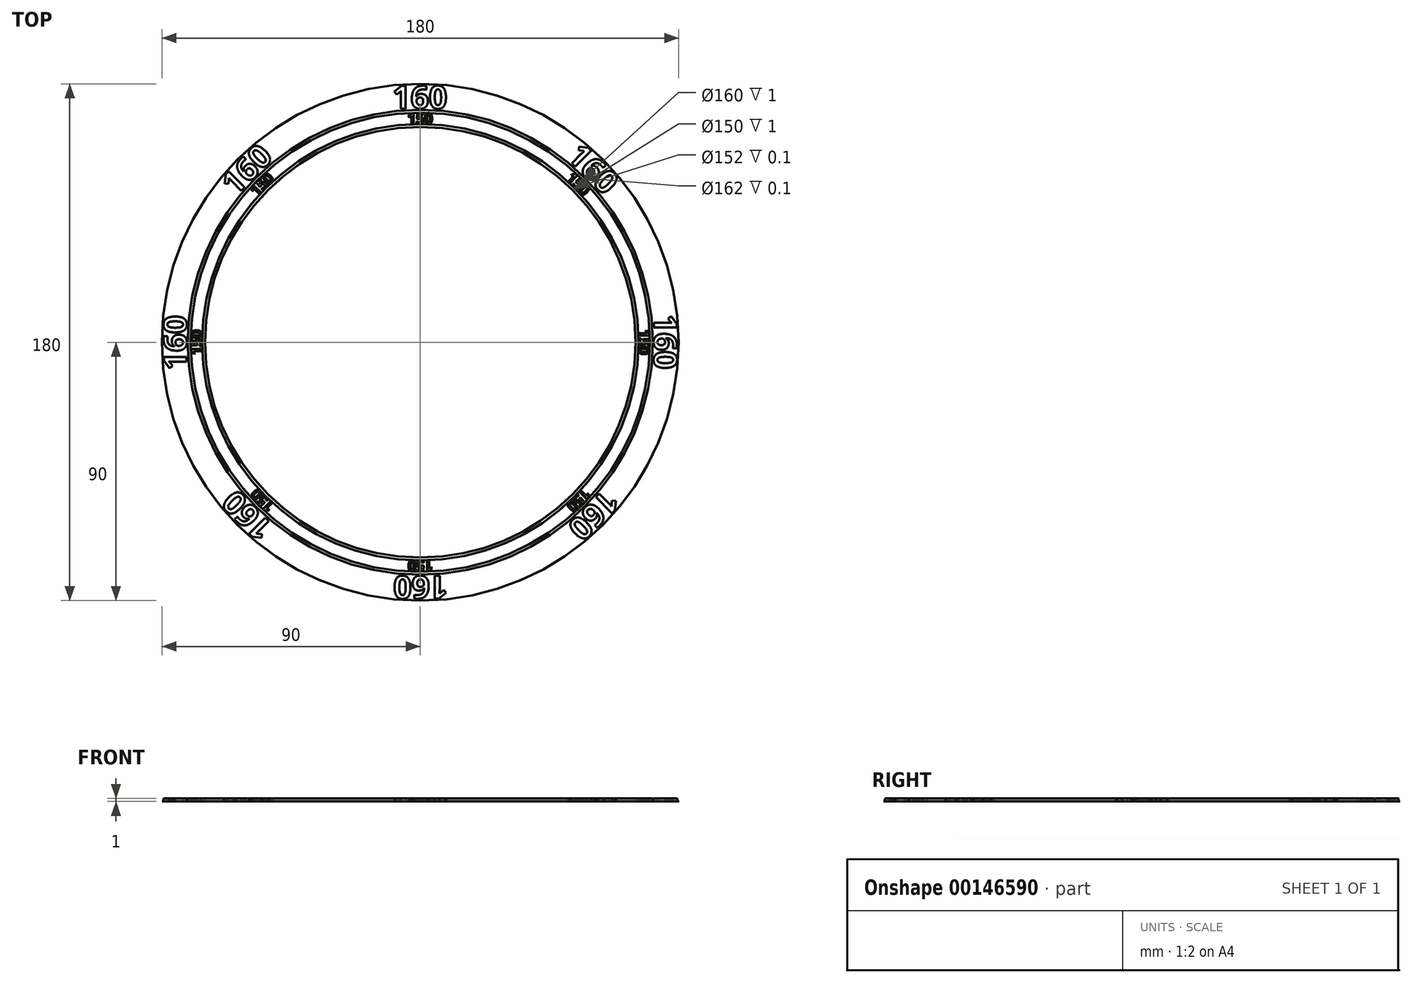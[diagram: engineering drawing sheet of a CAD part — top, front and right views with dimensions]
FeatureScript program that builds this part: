
annotation { "Feature Type Name" : "Feature", "Feature Type Description" : "" }
export const myFeature = defineFeature(function(context is Context, id is Id, definition is map)
    precondition{}
    {
        {
            var Q0;
            Q0=qCreatedBy(makeId("Top.planeOp"),FACE);
            var sketch = newSketch(context, id + "F0", { "sketchPlane" : qUnion([Q0])});
            skCircle(sketch, "E0", {"center": v(0, 0) * mm, "radius": 80 * mm});
            skCircle(sketch, "E1", {"center": v(0, 0) * mm, "radius": 75 * mm});
            skCircle(sketch, "E2", {"center": v(0, 0) * mm, "radius": 90 * mm});
            skCircle(sketch, "E3", {"center": v(0, 0) * mm, "radius": 100 * mm});
            skCircle(sketch, "E4", {"center": v(0, 0) * mm, "radius": 76 * mm});
            skCircle(sketch, "E5", {"center": v(0, 0) * mm, "radius": 81 * mm});
            skCircle(sketch, "E6", {"center": v(0, 0) * mm, "radius": 91 * mm});
            skSolve(sketch);
        }
        {
            var Q0;
            Q0=makeQuery(id+"F0.imprint","IMPRINT",FACE,{"disambiguationData":[TD([[makeQuery(id+"F0.imprint","IMPRINT",EDGE,{"derivedFrom":sQuery(id+"F0.wireOp",EDGE,"E1")}),-1.0]])]});
            var Q1;
            Q1=makeQuery(id+"F0.imprint","IMPRINT",FACE,{"disambiguationData":[TD([[makeQuery(id+"F0.imprint","IMPRINT",EDGE,{"derivedFrom":sQuery(id+"F0.wireOp",EDGE,"E0")}),-1.0]])]});
            extrude(context, id + "F1", {"entities" : qUnion([Q0, Q1]), "depth" : 1 * mm});
        }
        {
            var Q0;
            Q0=makeQuery(id+"F0.imprint","IMPRINT",FACE,{"disambiguationData":[TD([[makeQuery(id+"F0.imprint","IMPRINT",EDGE,{"derivedFrom":sQuery(id+"F0.wireOp",EDGE,"E1")}),1.0]])]});
            var sketch = newSketch(context, id + "F2", { "sketchPlane" : qUnion([Q0])});
            skText(sketch, "E7", { "text": "150", "fontName": "OpenSans-Bold.ttf"});
            skText(sketch, "E8", { "text": "160", "fontName": "OpenSans-Bold.ttf"});
            const initialGuessF2  = {"E7": [-0.00447, 0.07608, 1, 0, 0.0037], "E8": [-0.00968, 0.08139, 1, 0, 0.008]};
            skSetInitialGuess(sketch, initialGuessF2);
            skSolve(sketch);
        }
        {
            var Q0;
            Q0 = qSketchRegion(id + "F2", true);
            var Q1;
            Q1 = qConstructionFilter(qBodyType(qCreatedBy(id + "F2" ,EDGE), BodyType.WIRE), ConstructionObject.NO);
            extrude(context, id + "F3", {"entities" : qUnion([Q0]), "surfaceEntities" : qUnion([Q1]), "depth" : 1 * mm});
        }
        {
            var Q0;
            Q0=makeQuery(id+"F3.opExtrude","SWEPT_BODY",BODY,{"disambiguationData":[OSD([sQuery(id+"F2.wireOp",EDGE,"E8.sketch_text.stroke-35"),sQuery(id+"F2.wireOp",EDGE,"E8.sketch_text.stroke-36"),sQuery(id+"F2.wireOp",EDGE,"E8.sketch_text.stroke-37"),sQuery(id+"F2.wireOp",EDGE,"E8.sketch_text.stroke-38"),sQuery(id+"F2.wireOp",EDGE,"E8.sketch_text.stroke-39"),sQuery(id+"F2.wireOp",EDGE,"E8.sketch_text.stroke-40"),sQuery(id+"F2.wireOp",EDGE,"E8.sketch_text.stroke-41"),sQuery(id+"F2.wireOp",EDGE,"E8.sketch_text.stroke-42"),sQuery(id+"F2.wireOp",EDGE,"E8.sketch_text.stroke-43"),sQuery(id+"F2.wireOp",EDGE,"E8.sketch_text.stroke-44"),sQuery(id+"F2.wireOp",EDGE,"E8.sketch_text.stroke-45"),sQuery(id+"F2.wireOp",EDGE,"E8.sketch_text.stroke-46"),sQuery(id+"F2.wireOp",EDGE,"E8.sketch_text.stroke-47"),sQuery(id+"F2.wireOp",EDGE,"E8.sketch_text.stroke-48"),sQuery(id+"F2.wireOp",EDGE,"E8.sketch_text.stroke-49"),sQuery(id+"F2.wireOp",EDGE,"E8.sketch_text.stroke-50")])]});
            var Q1;
            Q1=makeQuery(id+"F3.opExtrude","SWEPT_BODY",BODY,{"disambiguationData":[OSD([sQuery(id+"F2.wireOp",EDGE,"E8.sketch_text.stroke-0"),sQuery(id+"F2.wireOp",EDGE,"E8.sketch_text.stroke-1"),sQuery(id+"F2.wireOp",EDGE,"E8.sketch_text.stroke-2"),sQuery(id+"F2.wireOp",EDGE,"E8.sketch_text.stroke-3"),sQuery(id+"F2.wireOp",EDGE,"E8.sketch_text.stroke-4"),sQuery(id+"F2.wireOp",EDGE,"E8.sketch_text.stroke-5"),sQuery(id+"F2.wireOp",EDGE,"E8.sketch_text.stroke-6"),sQuery(id+"F2.wireOp",EDGE,"E8.sketch_text.stroke-7"),sQuery(id+"F2.wireOp",EDGE,"E8.sketch_text.stroke-8"),sQuery(id+"F2.wireOp",EDGE,"E8.sketch_text.stroke-9")])]});
            var Q2;
            Q2=makeQuery(id+"F3.opExtrude","SWEPT_BODY",BODY,{"disambiguationData":[OSD([sQuery(id+"F2.wireOp",EDGE,"E8.sketch_text.stroke-10"),sQuery(id+"F2.wireOp",EDGE,"E8.sketch_text.stroke-11"),sQuery(id+"F2.wireOp",EDGE,"E8.sketch_text.stroke-12"),sQuery(id+"F2.wireOp",EDGE,"E8.sketch_text.stroke-13"),sQuery(id+"F2.wireOp",EDGE,"E8.sketch_text.stroke-14"),sQuery(id+"F2.wireOp",EDGE,"E8.sketch_text.stroke-15"),sQuery(id+"F2.wireOp",EDGE,"E8.sketch_text.stroke-16"),sQuery(id+"F2.wireOp",EDGE,"E8.sketch_text.stroke-17"),sQuery(id+"F2.wireOp",EDGE,"E8.sketch_text.stroke-18"),sQuery(id+"F2.wireOp",EDGE,"E8.sketch_text.stroke-19"),sQuery(id+"F2.wireOp",EDGE,"E8.sketch_text.stroke-20"),sQuery(id+"F2.wireOp",EDGE,"E8.sketch_text.stroke-21"),sQuery(id+"F2.wireOp",EDGE,"E8.sketch_text.stroke-22"),sQuery(id+"F2.wireOp",EDGE,"E8.sketch_text.stroke-23"),sQuery(id+"F2.wireOp",EDGE,"E8.sketch_text.stroke-24"),sQuery(id+"F2.wireOp",EDGE,"E8.sketch_text.stroke-25"),sQuery(id+"F2.wireOp",EDGE,"E8.sketch_text.stroke-26"),sQuery(id+"F2.wireOp",EDGE,"E8.sketch_text.stroke-27"),sQuery(id+"F2.wireOp",EDGE,"E8.sketch_text.stroke-28"),sQuery(id+"F2.wireOp",EDGE,"E8.sketch_text.stroke-29"),sQuery(id+"F2.wireOp",EDGE,"E8.sketch_text.stroke-30"),sQuery(id+"F2.wireOp",EDGE,"E8.sketch_text.stroke-31"),sQuery(id+"F2.wireOp",EDGE,"E8.sketch_text.stroke-32"),sQuery(id+"F2.wireOp",EDGE,"E8.sketch_text.stroke-33"),sQuery(id+"F2.wireOp",EDGE,"E8.sketch_text.stroke-34")])]});
            var Q3;
            Q3=makeQuery(id+"F3.opExtrude","SWEPT_BODY",BODY,{"disambiguationData":[OSD([sQuery(id+"F2.wireOp",EDGE,"E7.sketch_text.stroke-10"),sQuery(id+"F2.wireOp",EDGE,"E7.sketch_text.stroke-11"),sQuery(id+"F2.wireOp",EDGE,"E7.sketch_text.stroke-12"),sQuery(id+"F2.wireOp",EDGE,"E7.sketch_text.stroke-13"),sQuery(id+"F2.wireOp",EDGE,"E7.sketch_text.stroke-14"),sQuery(id+"F2.wireOp",EDGE,"E7.sketch_text.stroke-15"),sQuery(id+"F2.wireOp",EDGE,"E7.sketch_text.stroke-16"),sQuery(id+"F2.wireOp",EDGE,"E7.sketch_text.stroke-17"),sQuery(id+"F2.wireOp",EDGE,"E7.sketch_text.stroke-18"),sQuery(id+"F2.wireOp",EDGE,"E7.sketch_text.stroke-19"),sQuery(id+"F2.wireOp",EDGE,"E7.sketch_text.stroke-20"),sQuery(id+"F2.wireOp",EDGE,"E7.sketch_text.stroke-21"),sQuery(id+"F2.wireOp",EDGE,"E7.sketch_text.stroke-22"),sQuery(id+"F2.wireOp",EDGE,"E7.sketch_text.stroke-23"),sQuery(id+"F2.wireOp",EDGE,"E7.sketch_text.stroke-24"),sQuery(id+"F2.wireOp",EDGE,"E7.sketch_text.stroke-25"),sQuery(id+"F2.wireOp",EDGE,"E7.sketch_text.stroke-26"),sQuery(id+"F2.wireOp",EDGE,"E7.sketch_text.stroke-27"),sQuery(id+"F2.wireOp",EDGE,"E7.sketch_text.stroke-28"),sQuery(id+"F2.wireOp",EDGE,"E7.sketch_text.stroke-29")])]});
            var Q4;
            Q4=makeQuery(id+"F3.opExtrude","SWEPT_BODY",BODY,{"disambiguationData":[OSD([sQuery(id+"F2.wireOp",EDGE,"E7.sketch_text.stroke-0"),sQuery(id+"F2.wireOp",EDGE,"E7.sketch_text.stroke-1"),sQuery(id+"F2.wireOp",EDGE,"E7.sketch_text.stroke-2"),sQuery(id+"F2.wireOp",EDGE,"E7.sketch_text.stroke-3"),sQuery(id+"F2.wireOp",EDGE,"E7.sketch_text.stroke-4"),sQuery(id+"F2.wireOp",EDGE,"E7.sketch_text.stroke-5"),sQuery(id+"F2.wireOp",EDGE,"E7.sketch_text.stroke-6"),sQuery(id+"F2.wireOp",EDGE,"E7.sketch_text.stroke-7"),sQuery(id+"F2.wireOp",EDGE,"E7.sketch_text.stroke-8"),sQuery(id+"F2.wireOp",EDGE,"E7.sketch_text.stroke-9")])]});
            var Q5;
            Q5=makeQuery(id+"F3.opExtrude","SWEPT_BODY",BODY,{"disambiguationData":[OSD([sQuery(id+"F2.wireOp",EDGE,"E7.sketch_text.stroke-30"),sQuery(id+"F2.wireOp",EDGE,"E7.sketch_text.stroke-31"),sQuery(id+"F2.wireOp",EDGE,"E7.sketch_text.stroke-32"),sQuery(id+"F2.wireOp",EDGE,"E7.sketch_text.stroke-33"),sQuery(id+"F2.wireOp",EDGE,"E7.sketch_text.stroke-34"),sQuery(id+"F2.wireOp",EDGE,"E7.sketch_text.stroke-35"),sQuery(id+"F2.wireOp",EDGE,"E7.sketch_text.stroke-36"),sQuery(id+"F2.wireOp",EDGE,"E7.sketch_text.stroke-37"),sQuery(id+"F2.wireOp",EDGE,"E7.sketch_text.stroke-38"),sQuery(id+"F2.wireOp",EDGE,"E7.sketch_text.stroke-39"),sQuery(id+"F2.wireOp",EDGE,"E7.sketch_text.stroke-40"),sQuery(id+"F2.wireOp",EDGE,"E7.sketch_text.stroke-41"),sQuery(id+"F2.wireOp",EDGE,"E7.sketch_text.stroke-42"),sQuery(id+"F2.wireOp",EDGE,"E7.sketch_text.stroke-43"),sQuery(id+"F2.wireOp",EDGE,"E7.sketch_text.stroke-44"),sQuery(id+"F2.wireOp",EDGE,"E7.sketch_text.stroke-45")])]});
            var Q6;
            Q6=sQuery(id+"F0.wireOp",EDGE,"E1");
            circularPattern(context, id + "F4", {"entities" : qUnion([Q0, Q1, Q2, Q3, Q4, Q5]), "axis" : qUnion([Q6]), "angle" : 45 * degree, "instanceCount" : 8});
        }
        {
            var Q0;
            Q0=makeQuery(id+"F0.imprint","IMPRINT",FACE,{"disambiguationData":[TD([[makeQuery(id+"F0.imprint","IMPRINT",EDGE,{"derivedFrom":sQuery(id+"F0.wireOp",EDGE,"E2")}),1.0]])]});
            var Q1;
            Q1=makeQuery(id+"F0.imprint","IMPRINT",FACE,{"disambiguationData":[TD([[makeQuery(id+"F0.imprint","IMPRINT",EDGE,{"derivedFrom":sQuery(id+"F0.wireOp",EDGE,"E0")}),1.0]])]});
            extrude(context, id + "F5", {"entities" : qUnion([Q0, Q1]), "depth" : 0.1 * mm});
        }
    });
